# Revit family: XAL MoveIt46
name_source: partatom
category: Lighting Fixtures
revit_build: Autodesk Revit 2014 (Build: 20140709_2115(x64)
units: mm (PartAtom-declared; Revit-internal decimal feet)

## types (1)
- XAL MoveIT 45
    Apparent Load = 4 VA
    Assembly Code = D5020200
    Color Filter = 16777215
    Cutout Length = 1' - 1 7/8"
    Cutout Offset = 0' - 6 15/16"
    Cutout Width = 0' - 9 7/8"
    Default Elevation = 0' - 0"
    Description = Recessed Lensed LED Luminaire with adjustable extension aperture
    Diameter = 0' - 1 3/4"
    Dimming = DIM 0-10V
    Dimming Lamp Color Temperature Shift = <None>
    Emit Shape Visible in Rendering = No
    Emit from Circle Diameter = 0' - 1 9/16"
    Feeder Length = 10' - 0"
    Height = 0' - 2 1/4"
    Installation = Recessed
    Lamp = LED White
    Lamp Quantity = 3
    Lens Material = XAL - Lens, Lit
    Lens Radius = 0' - 0 25/32"
    Manufacturer = XAL, Inc.
    Model = Use Type Catalog or Enter Manually
    Optic = Flood
    Output = 4W
    Photometric Web File = MOV411117131051L68.ies
    R1 Void = 0' - 0"
    R2 = Yes
    R2 Void = 0' - 0"
    R3 = Yes
    R3 Void = 0' - 0"
    Radius = 0' - 0 7/8"
    Range = MOVEIT 45
    RoundLED = Yes
    S1 Void = 0' - 4"
    S2 = No
    S2 Void = 0' - 4"
    S3 = No
    S3 Void = 0' - 4"
    Shape = Round LED
    SquareLED = No
    Tilt Angle = -90.00°
    Trim = Sheet Rock Trimless
    Trim Material = XAL - White
    URL = http://www.xalusa.com
    Voltage = 14 V
    Voltage Code = 14V / 350mA

## geometry (parser evidence)
native form markers: Blend x10, Sweep x2
no freeform markers — native parametric forms only
